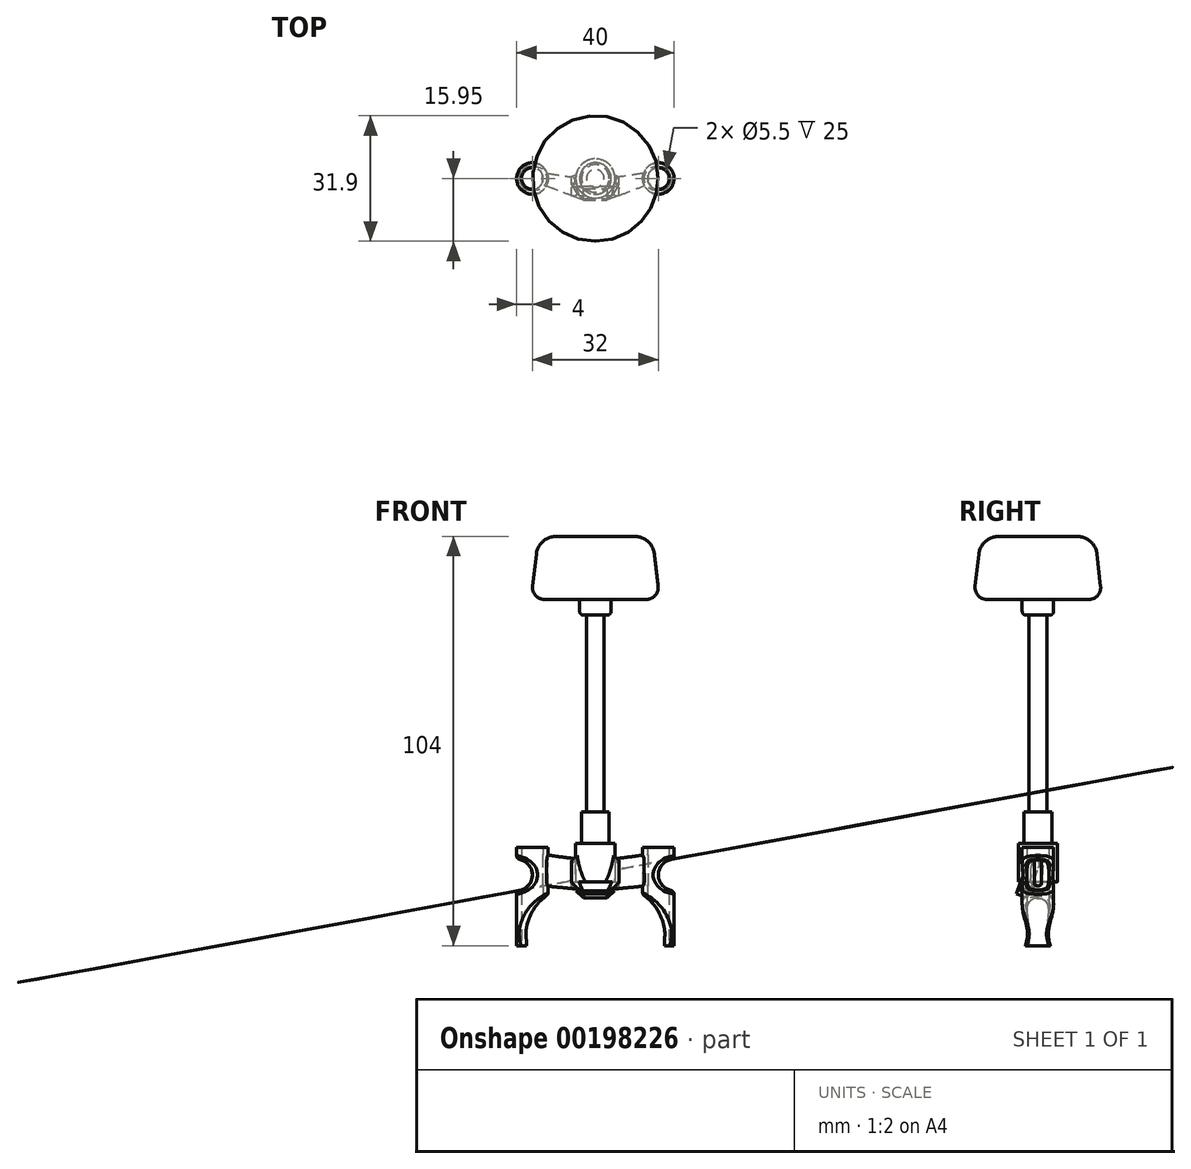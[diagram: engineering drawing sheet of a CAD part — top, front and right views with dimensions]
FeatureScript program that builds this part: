
annotation { "Feature Type Name" : "Feature", "Feature Type Description" : "" }
export const myFeature = defineFeature(function(context is Context, id is Id, definition is map)
    precondition{}
    {
        {
            var Q0;
            Q0=qCreatedBy(makeId("Top.planeOp"),FACE);
            var sketch = newSketch(context, id + "F0", { "sketchPlane" : qUnion([Q0])});
            skCircle(sketch, "E0", {"center": v(-16, 0) * mm, "radius": 2.75 * mm});
            skCircle(sketch, "E1", {"center": v(16, 0) * mm, "radius": 2.75 * mm});
            skCircle(sketch, "E2", {"center": v(-16, 0) * mm, "radius": 4 * mm});
            skCircle(sketch, "E3", {"center": v(16, 0) * mm, "radius": 4 * mm});
            skSolve(sketch);
        }
        {
            var Q0;
            Q0 = qSketchRegion(id + "F0", true);
            extrude(context, id + "F1", {"entities" : qUnion([Q0]), "depth" : 11 * mm});
        }
        {
            var Q0;
            Q0=qCreatedBy(makeId("Right.planeOp"),FACE);
            var sketch = newSketch(context, id + "F2", { "sketchPlane" : qUnion([Q0])});
            skLineSegment(sketch, "E4.bottom", {"start": v(-5.42, -0.75) * mm, "end": v(-2.6, -1.78) * mm});
            skLineSegment(sketch, "E4.top", {"start": v(-1.32, 10.53) * mm, "end": v(1.5, 9.5) * mm});
            skLineSegment(sketch, "E4.left", {"start": v(-5.42, -0.75) * mm, "end": v(-1.32, 10.53) * mm});
            skLineSegment(sketch, "E4.right", {"start": v(-2.6, -1.78) * mm, "end": v(1.5, 9.5) * mm});
            skPoint(sketch, "E4.middle", {"position": v(-1.96, 4.37) * mm});
            skSolve(sketch);
        }
        {
            var Q0;
            Q0 = qSketchRegion(id + "F2", true);
            var Q1;
            Q1=makeQuery(id+"F1.opExtrude","SWEPT_FACE",FACE,{"disambiguationData":[OSD([sQuery(id+"F0.wireOp",EDGE,"E3")])]});
            var Q2;
            Q2=makeQuery(id+"F1.opExtrude","SWEPT_BODY",BODY,{"disambiguationData":[OSD([sQuery(id+"F0.wireOp",EDGE,"E1"),sQuery(id+"F0.wireOp",EDGE,"E3")])]});
            extrude(context, id + "F3", {"entities" : qUnion([Q0]), "operationType" : NewBodyOperationType.ADD, "endBound" : BoundingType.SYMMETRIC, "oppositeDirection" : true, "endBoundEntityFace" : qUnion([Q1]), "endBoundEntityBody" : qUnion([Q2]), "depth" : 12 * mm});
        }
        {
            var Q0;
            Q0=qCreatedBy(makeId("Right.planeOp"),FACE);
            cPlane(context, id + "F4", {"entities" : qUnion([Q0]), "cplaneType" : CPlaneType.OFFSET, "offset" : (16 - 2.6) * mm, "oppositeDirection" : true, "width" : 150 * mm, "height" : 150 * mm});
        }
        {
            var Q0;
            Q0=qCreatedBy(id+"F4.planeOp",FACE);
            var sketch = newSketch(context, id + "F5", { "sketchPlane" : qUnion([Q0])});
            skLineSegment(sketch, "E5.bottom", {"start": v(0, 1.25) * mm, "end": v(0, 1.25) * mm});
            skLineSegment(sketch, "E5.top", {"start": v(0, 9.25) * mm, "end": v(0, 9.25) * mm});
            skLineSegment(sketch, "E5.left", {"start": v(1.5, 2.75) * mm, "end": v(1.5, 7.75) * mm});
            skLineSegment(sketch, "E5.right", {"start": v(-1.5, 2.75) * mm, "end": v(-1.5, 7.75) * mm});
            skPoint(sketch, "E5.middle", {"position": v(0, 5.25) * mm});
            skPoint(sketch, "E6.visualSharp", {"position": v(-1.5, 9.25) * mm});
            skArc(sketch, "E6.filletArc", {"start": v(0, 9.25) * mm, "mid": v(-1.06, 8.81) * mm, "end": v(-1.5, 7.75) * mm});
            skPoint(sketch, "E7.visualSharp", {"position": v(1.5, 9.25) * mm});
            skArc(sketch, "E7.filletArc", {"start": v(1.5, 7.75) * mm, "mid": v(1.06, 8.81) * mm, "end": v(0, 9.25) * mm});
            skPoint(sketch, "E8.visualSharp", {"position": v(-1.5, 1.25) * mm});
            skArc(sketch, "E8.filletArc", {"start": v(-1.5, 2.75) * mm, "mid": v(-1.06, 1.69) * mm, "end": v(0, 1.25) * mm});
            skPoint(sketch, "E9.visualSharp", {"position": v(1.5, 1.25) * mm});
            skArc(sketch, "E9.filletArc", {"start": v(0, 1.25) * mm, "mid": v(1.06, 1.69) * mm, "end": v(1.5, 2.75) * mm});
            skSolve(sketch);
        }
        {
            var Q0;
            Q0=makeQuery(id+"F3.opExtrude","CAP_FACE",FACE,{"disambiguationData":[OSD([sQuery(id+"F2.wireOp",EDGE,"E4.bottom"),sQuery(id+"F2.wireOp",EDGE,"E4.top"),sQuery(id+"F2.wireOp",EDGE,"E4.left"),sQuery(id+"F2.wireOp",EDGE,"E4.right")])],"isStart":false});
            var sketch = newSketch(context, id + "F6", { "sketchPlane" : qUnion([Q0])});
            skLineSegment(sketch, "E10", {"start": v(0.6, 8.13) * mm, "end": v(0.6, 8.13) * mm});
            skLineSegment(sketch, "E11", {"start": v(2.52, 7.24) * mm, "end": v(4.23, 2.54) * mm});
            skLineSegment(sketch, "E12", {"start": v(3.33, 0.62) * mm, "end": v(3.33, 0.62) * mm});
            skLineSegment(sketch, "E13", {"start": v(1.4, 1.51) * mm, "end": v(-0.3, 6.21) * mm});
            skPoint(sketch, "E14.visualSharp", {"position": v(-0.82, 7.62) * mm});
            skArc(sketch, "E14.filletArc", {"start": v(0.6, 8.13) * mm, "mid": v(-0.25, 7.36) * mm, "end": v(-0.3, 6.21) * mm});
            skPoint(sketch, "E15.visualSharp", {"position": v(2, 8.65) * mm});
            skArc(sketch, "E15.filletArc", {"start": v(2.52, 7.24) * mm, "mid": v(1.74, 8.08) * mm, "end": v(0.6, 8.13) * mm});
            skPoint(sketch, "E16.visualSharp", {"position": v(4.74, 1.13) * mm});
            skArc(sketch, "E16.filletArc", {"start": v(3.33, 0.62) * mm, "mid": v(4.18, 1.4) * mm, "end": v(4.23, 2.54) * mm});
            skPoint(sketch, "E17.visualSharp", {"position": v(1.92, 0.1) * mm});
            skArc(sketch, "E17.filletArc", {"start": v(1.4, 1.51) * mm, "mid": v(2.18, 0.67) * mm, "end": v(3.33, 0.62) * mm});
            skSolve(sketch);
        }
        {
            var Q2;
            Q2 = qSketchRegion(id + "F6", true);
            var Q3;
            Q3 = qSketchRegion(id + "F5", true);
            loft(context, id + "F7", {"operationType" : NewBodyOperationType.ADD, "sheetProfilesArray" : [{ "sheetProfileEntities" : qUnion([Q2]) }, { "sheetProfileEntities" : qUnion([Q3]) }]});
        }
        {
            var Q0;
            Q0=makeQuery(id+"F3.opExtrude","CAP_FACE",FACE,{"disambiguationData":[OSD([sQuery(id+"F2.wireOp",EDGE,"E4.bottom"),sQuery(id+"F2.wireOp",EDGE,"E4.top"),sQuery(id+"F2.wireOp",EDGE,"E4.left"),sQuery(id+"F2.wireOp",EDGE,"E4.right")])],"isStart":true});
            var sketch = newSketch(context, id + "F8", { "sketchPlane" : qUnion([Q0])});
            skLineSegment(sketch, "E18", {"start": v(-0.6, 8.13) * mm, "end": v(-0.6, 8.13) * mm});
            skLineSegment(sketch, "E19", {"start": v(0.3, 6.21) * mm, "end": v(-1.4, 1.51) * mm});
            skLineSegment(sketch, "E20", {"start": v(-3.33, 0.62) * mm, "end": v(-3.33, 0.62) * mm});
            skLineSegment(sketch, "E21", {"start": v(-4.23, 2.54) * mm, "end": v(-2.52, 7.24) * mm});
            skPoint(sketch, "E22.visualSharp", {"position": v(-2, 8.65) * mm});
            skArc(sketch, "E22.filletArc", {"start": v(-0.6, 8.13) * mm, "mid": v(-1.74, 8.08) * mm, "end": v(-2.52, 7.24) * mm});
            skPoint(sketch, "E23.visualSharp", {"position": v(0.82, 7.62) * mm});
            skArc(sketch, "E23.filletArc", {"start": v(0.3, 6.21) * mm, "mid": v(0.25, 7.36) * mm, "end": v(-0.6, 8.13) * mm});
            skPoint(sketch, "E24.visualSharp", {"position": v(-4.74, 1.13) * mm});
            skArc(sketch, "E24.filletArc", {"start": v(-4.23, 2.54) * mm, "mid": v(-4.18, 1.4) * mm, "end": v(-3.33, 0.62) * mm});
            skPoint(sketch, "E25.visualSharp", {"position": v(-1.92, 0.1) * mm});
            skArc(sketch, "E25.filletArc", {"start": v(-3.33, 0.62) * mm, "mid": v(-2.18, 0.67) * mm, "end": v(-1.4, 1.51) * mm});
            skSolve(sketch);
        }
        {
            var Q0;
            Q0=qCreatedBy(makeId("Right.planeOp"),FACE);
            cPlane(context, id + "F9", {"entities" : qUnion([Q0]), "cplaneType" : CPlaneType.OFFSET, "offset" : 13.4 * mm, "width" : 150 * mm, "height" : 150 * mm});
        }
        {
            var Q0;
            Q0=qCreatedBy(id+"F9.planeOp",FACE);
            var sketch = newSketch(context, id + "F10", { "sketchPlane" : qUnion([Q0])});
            skLineSegment(sketch, "E26.bottom", {"start": v(0, 9.25) * mm, "end": v(0, 9.25) * mm});
            skLineSegment(sketch, "E26.top", {"start": v(0, 1.25) * mm, "end": v(0, 1.25) * mm});
            skLineSegment(sketch, "E26.left", {"start": v(-1.5, 7.75) * mm, "end": v(-1.5, 2.75) * mm});
            skLineSegment(sketch, "E26.right", {"start": v(1.5, 7.75) * mm, "end": v(1.5, 2.75) * mm});
            skPoint(sketch, "E27.visualSharp", {"position": v(-1.5, 9.25) * mm});
            skArc(sketch, "E27.filletArc", {"start": v(0, 9.25) * mm, "mid": v(-1.06, 8.81) * mm, "end": v(-1.5, 7.75) * mm});
            skPoint(sketch, "E28.visualSharp", {"position": v(1.5, 9.25) * mm});
            skArc(sketch, "E28.filletArc", {"start": v(1.5, 7.75) * mm, "mid": v(1.06, 8.81) * mm, "end": v(0, 9.25) * mm});
            skPoint(sketch, "E29.visualSharp", {"position": v(-1.5, 1.25) * mm});
            skArc(sketch, "E29.filletArc", {"start": v(-1.5, 2.75) * mm, "mid": v(-1.06, 1.69) * mm, "end": v(0, 1.25) * mm});
            skPoint(sketch, "E30.visualSharp", {"position": v(1.5, 1.25) * mm});
            skArc(sketch, "E30.filletArc", {"start": v(0, 1.25) * mm, "mid": v(1.06, 1.69) * mm, "end": v(1.5, 2.75) * mm});
            skSolve(sketch);
        }
        {
            var Q2;
            Q2 = qSketchRegion(id + "F8", true);
            var Q3;
            Q3 = qSketchRegion(id + "F10", true);
            loft(context, id + "F11", {"operationType" : NewBodyOperationType.ADD, "sheetProfilesArray" : [{ "sheetProfileEntities" : qUnion([Q2]) }, { "sheetProfileEntities" : qUnion([Q3]) }]});
        }
        {
            var Q0;
            Q0=makeQuery(id+"F3.opExtrude","SWEPT_FACE",FACE,{"disambiguationData":[OSD([sQuery(id+"F2.wireOp",EDGE,"E4.left")])]});
            var sketch = newSketch(context, id + "F12", { "sketchPlane" : qUnion([Q0])});
            skCircle(sketch, "E31", {"center": v(0, 3.44) * mm, "radius": 3.5 * mm});
            skSolve(sketch);
        }
        {
            var Q0;
            Q0=makeQuery(id+"F12.imprint","IMPRINT",FACE,{"disambiguationData":[TD([[makeQuery(id+"F12.imprint","IMPRINT",EDGE,{"derivedFrom":sQuery(id+"F12.wireOp",EDGE,"E31")}),1.0]])]});
            extrude(context, id + "F13", {"entities" : qUnion([Q0]), "operationType" : NewBodyOperationType.REMOVE, "oppositeDirection" : true, "depth" : 25 * mm});
        }
        {
            var Q0;
            Q0=makeQuery(id+"F3.opExtrude","CAP_EDGE",EDGE,{"disambiguationData":[OSD([sQuery(id+"F2.wireOp",EDGE,"E4.top")])],"isStart":false});
            var Q1;
            Q1=makeQuery(id+"F3.opExtrude","CAP_EDGE",EDGE,{"disambiguationData":[OSD([sQuery(id+"F2.wireOp",EDGE,"E4.top")])],"isStart":true});
            var Q2;
            Q2=makeQuery(id+"F3.opExtrude","CAP_EDGE",EDGE,{"disambiguationData":[OSD([sQuery(id+"F2.wireOp",EDGE,"E4.bottom")])],"isStart":true});
            var Q3;
            Q3=makeQuery(id+"F3.opExtrude","CAP_EDGE",EDGE,{"disambiguationData":[OSD([sQuery(id+"F2.wireOp",EDGE,"E4.bottom")])],"isStart":false});
            chamfer(context, id + "F14", {"entities" : qUnion([Q0, Q1, Q2, Q3]), "width" : 3 * mm, "tangentPropagation" : true});
        }
        {
            var Q0;
            Q0=qCreatedBy(makeId("Top.planeOp"),FACE);
            var sketch = newSketch(context, id + "F15", { "sketchPlane" : qUnion([Q0])});
            skCircle(sketch, "E32", {"center": v(0, 0) * mm, "radius": 3.5 * mm});
            skSolve(sketch);
        }
        {
            var Q0;
            Q0=makeQuery(id+"F15.imprint","IMPRINT",FACE,{"disambiguationData":[TD([[makeQuery(id+"F15.imprint","IMPRINT",EDGE,{"derivedFrom":sQuery(id+"F15.wireOp",EDGE,"E32")}),1.0]])]});
            extrude(context, id + "F16", {"entities" : qUnion([Q0]), "depth" : 20 * mm});
        }
        {
            var Q0;
            Q0=makeQuery(id+"F1.opExtrude","CAP_FACE",FACE,{"disambiguationData":[OSD([sQuery(id+"F0.wireOp",EDGE,"E0"),sQuery(id+"F0.wireOp",EDGE,"E2")])],"isStart":true});
            var Q1;
            Q1=makeQuery(id+"F1.opExtrude","CAP_FACE",FACE,{"disambiguationData":[OSD([sQuery(id+"F0.wireOp",EDGE,"E1"),sQuery(id+"F0.wireOp",EDGE,"E3")])],"isStart":true});
            extrude(context, id + "F17", {"entities" : qUnion([Q0, Q1]), "operationType" : NewBodyOperationType.ADD, "depth" : 14 * mm});
        }
        {
            var Q0;
            Q0=qCreatedBy(makeId("Front.planeOp"),FACE);
            var sketch = newSketch(context, id + "F18", { "sketchPlane" : qUnion([Q0])});
            skLineSegment(sketch, "E33", {"start": v(-17.5, -14) * mm, "end": v(-17.5, -11) * mm});
            skArc(sketch, "E34", {"start": v(-12, -1) * mm, "mid": v(-16.03, -5.3) * mm, "end": v(-17.5, -11) * mm});
            skLineSegment(sketch, "E35", {"start": v(-12, -1) * mm, "end": v(-12, -14) * mm});
            skLineSegment(sketch, "E36", {"start": v(-12, -14) * mm, "end": v(-17.5, -14) * mm});
            skPoint(sketch, "E37.orphan", {"position": v(-12, 0) * mm});
            skArc(sketch, "E38.MirrorCS", {"start": v(12, -1) * mm, "mid": v(16.03, -5.3) * mm, "end": v(17.5, -11) * mm});
            skPoint(sketch, "E39.MirrorP", {"position": v(12, 0) * mm});
            skLineSegment(sketch, "E40.MirrorCS", {"start": v(12, -1) * mm, "end": v(12, -14) * mm});
            skLineSegment(sketch, "E41.MirrorCS", {"start": v(17.5, -14) * mm, "end": v(17.5, -11) * mm});
            skLineSegment(sketch, "E42.MirrorCS", {"start": v(12, -14) * mm, "end": v(17.5, -14) * mm});
            skCircle(sketch, "E43", {"center": v(-20, 4) * mm, "radius": 4 * mm});
            skCircle(sketch, "E44.MirrorC", {"center": v(20, 4) * mm, "radius": 4 * mm});
            skSolve(sketch);
        }
        {
            var Q0;
            Q0 = qSketchRegion(id + "F18", true);
            extrude(context, id + "F19", {"entities" : qUnion([Q0]), "operationType" : NewBodyOperationType.REMOVE, "endBound" : BoundingType.SYMMETRIC, "oppositeDirection" : true, "depth" : 25 * mm});
        }
        {
            var Q0;
            {var subQ0=sQuery(id+"F0.wireOp",EDGE,"E2");Q0=makeQuery(id+"F19.boolean.opBoolean","INTERSECT",EDGE,{"disambiguationData":[OD(0.0)],"derivedFrom":[makeQuery(id+"F17.boolean.opBoolean","MERGE",FACE,{"derivedFrom":[makeQuery(id+"F1.opExtrude","SWEPT_FACE",FACE,{"disambiguationData":[OSD([subQ0])]}),makeQuery(id+"F17.opExtrude","SWEPT_FACE",FACE,{"disambiguationData":[OSD([subQ0])]})]}),makeQuery(id+"F19.opExtrude","SWEPT_FACE",FACE,{"disambiguationData":[OSD([sQuery(id+"F18.wireOp",EDGE,"E33")])]})]});}
            var Q1;
            {var subQ0=sQuery(id+"F0.wireOp",EDGE,"E2");Q1=makeQuery(id+"F19.boolean.opBoolean","INTERSECT",EDGE,{"derivedFrom":[makeQuery(id+"F17.boolean.opBoolean","MERGE",FACE,{"derivedFrom":[makeQuery(id+"F1.opExtrude","SWEPT_FACE",FACE,{"disambiguationData":[OSD([subQ0])]}),makeQuery(id+"F17.opExtrude","SWEPT_FACE",FACE,{"disambiguationData":[OSD([subQ0])]})]}),makeQuery(id+"F19.opExtrude","SWEPT_FACE",FACE,{"disambiguationData":[OSD([sQuery(id+"F18.wireOp",EDGE,"E34")])]})]});}
            var Q2;
            {var subQ0=sQuery(id+"F0.wireOp",EDGE,"E3");Q2=makeQuery(id+"F19.boolean.opBoolean","INTERSECT",EDGE,{"disambiguationData":[OD(0.0)],"derivedFrom":[makeQuery(id+"F17.boolean.opBoolean","MERGE",FACE,{"derivedFrom":[makeQuery(id+"F1.opExtrude","SWEPT_FACE",FACE,{"disambiguationData":[OSD([subQ0])]}),makeQuery(id+"F17.opExtrude","SWEPT_FACE",FACE,{"disambiguationData":[OSD([subQ0])]})]}),makeQuery(id+"F19.opExtrude","SWEPT_FACE",FACE,{"disambiguationData":[OSD([sQuery(id+"F18.wireOp",EDGE,"E41.MirrorCS")])]})]});}
            var Q3;
            {var subQ0=sQuery(id+"F0.wireOp",EDGE,"E3");Q3=makeQuery(id+"F19.boolean.opBoolean","INTERSECT",EDGE,{"derivedFrom":[makeQuery(id+"F17.boolean.opBoolean","MERGE",FACE,{"derivedFrom":[makeQuery(id+"F1.opExtrude","SWEPT_FACE",FACE,{"disambiguationData":[OSD([subQ0])]}),makeQuery(id+"F17.opExtrude","SWEPT_FACE",FACE,{"disambiguationData":[OSD([subQ0])]})]}),makeQuery(id+"F19.opExtrude","SWEPT_FACE",FACE,{"disambiguationData":[OSD([sQuery(id+"F18.wireOp",EDGE,"E38.MirrorCS")])]})]});}
            fillet(context, id + "F20", {"entities" : qUnion([Q0, Q1, Q2, Q3]), "radius" : 1 * mm, "tangentPropagation" : true, "allowEdgeOverflow" : false});
        }
        {
            var Q0;
            {var subQ0=sQuery(id+"F0.wireOp",EDGE,"E2");Q0=makeQuery(id+"F19.boolean.opBoolean","INTERSECT",EDGE,{"derivedFrom":[makeQuery(id+"F17.boolean.opBoolean","MERGE",FACE,{"derivedFrom":[makeQuery(id+"F1.opExtrude","SWEPT_FACE",FACE,{"disambiguationData":[OSD([subQ0])]}),makeQuery(id+"F17.opExtrude","SWEPT_FACE",FACE,{"disambiguationData":[OSD([subQ0])]})]}),makeQuery(id+"F19.opExtrude","SWEPT_FACE",FACE,{"disambiguationData":[OSD([sQuery(id+"F18.wireOp",EDGE,"E43")])]})]});}
            var Q1;
            {var subQ0=sQuery(id+"F0.wireOp",EDGE,"E3");Q1=makeQuery(id+"F19.boolean.opBoolean","INTERSECT",EDGE,{"derivedFrom":[makeQuery(id+"F17.boolean.opBoolean","MERGE",FACE,{"derivedFrom":[makeQuery(id+"F1.opExtrude","SWEPT_FACE",FACE,{"disambiguationData":[OSD([subQ0])]}),makeQuery(id+"F17.opExtrude","SWEPT_FACE",FACE,{"disambiguationData":[OSD([subQ0])]})]}),makeQuery(id+"F19.opExtrude","SWEPT_FACE",FACE,{"disambiguationData":[OSD([sQuery(id+"F18.wireOp",EDGE,"E44.MirrorC")])]})]});}
            fillet(context, id + "F21", {"entities" : qUnion([Q0, Q1]), "radius" : 1 * mm, "tangentPropagation" : true, "allowEdgeOverflow" : false});
        }
        {
            var Q0;
            Q0=qCreatedBy(makeId("Top.planeOp"),FACE);
            var sketch = newSketch(context, id + "F22", { "sketchPlane" : qUnion([Q0])});
            skCircle(sketch, "E45", {"center": v(0, 0) * mm, "radius": 5 * mm});
            skSolve(sketch);
        }
        {
            var Q0;
            Q0 = qSketchRegion(id + "F22", true);
            extrude(context, id + "F23", {"entities" : qUnion([Q0]), "operationType" : NewBodyOperationType.ADD, "depth" : 12 * mm});
        }
        {
            var Q0;
            Q0=makeQuery(id+"F16.opExtrude","CAP_FACE",FACE,{"disambiguationData":[OSD([sQuery(id+"F15.wireOp",EDGE,"E32")])],"isStart":false});
            var sketch = newSketch(context, id + "F24", { "sketchPlane" : qUnion([Q0])});
            skCircle(sketch, "E46", {"center": v(0, 0) * mm, "radius": 2.25 * mm});
            skSolve(sketch);
        }
        {
            var Q0;
            Q0=makeQuery(id+"F24.imprint","IMPRINT",FACE,{"disambiguationData":[TD([[makeQuery(id+"F24.imprint","IMPRINT",EDGE,{"derivedFrom":sQuery(id+"F24.wireOp",EDGE,"E46")}),1.0]])]});
            extrude(context, id + "F25", {"entities" : qUnion([Q0]), "operationType" : NewBodyOperationType.ADD, "depth" : 55 * mm});
        }
        {
            var Q0;
            Q0=qCreatedBy(makeId("Front.planeOp"),FACE);
            var sketch = newSketch(context, id + "F26", { "sketchPlane" : qUnion([Q0])});
            skLineSegment(sketch, "E47", {"start": v(0, 90) * mm, "end": v(10.03, 90) * mm});
            skLineSegment(sketch, "E48", {"start": v(0, 70) * mm, "end": v(3, 70) * mm});
            skLineSegment(sketch, "E49", {"start": v(0, 70) * mm, "end": v(0, 90) * mm, "construction": true});
            skLineSegment(sketch, "E50", {"start": v(4, 71) * mm, "end": v(4, 73.5) * mm});
            skLineSegment(sketch, "E51", {"start": v(4.5, 74) * mm, "end": v(12.95, 74) * mm});
            skArc(sketch, "E52.filletArc", {"start": v(12.95, 74) * mm, "mid": v(15.2, 75) * mm, "end": v(15.93, 77.34) * mm});
            skLineSegment(sketch, "E53", {"start": v(15.93, 77.34) * mm, "end": v(15, 85.56) * mm});
            skPoint(sketch, "E54.visualSharp", {"position": v(14.5, 90) * mm});
            skArc(sketch, "E54.filletArc", {"start": v(15, 85.56) * mm, "mid": v(13.37, 88.73) * mm, "end": v(10.03, 90) * mm});
            skLineSegment(sketch, "E55", {"start": v(0, 90) * mm, "end": v(0, 70) * mm});
            skPoint(sketch, "E56.visualSharp", {"position": v(4, 70) * mm});
            skArc(sketch, "E56.filletArc", {"start": v(3, 70) * mm, "mid": v(3.7, 70.3) * mm, "end": v(4, 71) * mm});
            skPoint(sketch, "E57.visualSharp", {"position": v(4, 74) * mm});
            skArc(sketch, "E57.filletArc", {"start": v(4.5, 74) * mm, "mid": v(4.15, 73.85) * mm, "end": v(4, 73.5) * mm});
            skSolve(sketch);
        }
        {
            var Q0;
            Q0=makeQuery(id+"F26.imprint","IMPRINT",FACE,{"disambiguationData":[TD([[makeQuery(id+"F26.imprint","IMPRINT",EDGE,{"derivedFrom":sQuery(id+"F26.wireOp",EDGE,"E47")}),-1.0]])]});
            var Q1;
            Q1=sQuery(id+"F26.wireOp",EDGE,"E55");
            revolve(context, id + "F27", {"operationType" : NewBodyOperationType.ADD, "entities" : qUnion([Q0]), "axis" : qUnion([Q1]), "revolveType" : RevolveType.FULL});
        }
        {
            var Q0;
            Q0=qCreatedBy(makeId("Top.planeOp"),FACE);
            var sketch = newSketch(context, id + "F28", { "sketchPlane" : qUnion([Q0])});
            skCircle(sketch, "E58", {"center": v(0, 0) * mm, "radius": 6 * mm});
            skCircle(sketch, "E59", {"center": v(0, 0) * mm, "radius": 4 * mm});
            skSolve(sketch);
        }
        {
            var Q0;
            Q0=makeQuery(id+"F28.imprint","IMPRINT",FACE,{"disambiguationData":[TD([[makeQuery(id+"F28.imprint","IMPRINT",EDGE,{"derivedFrom":sQuery(id+"F28.wireOp",EDGE,"E58")}),1.0]])]});
            extrude(context, id + "F29", {"entities" : qUnion([Q0]), "operationType" : NewBodyOperationType.REMOVE, "depth" : 2.3 * mm});
        }
    });
